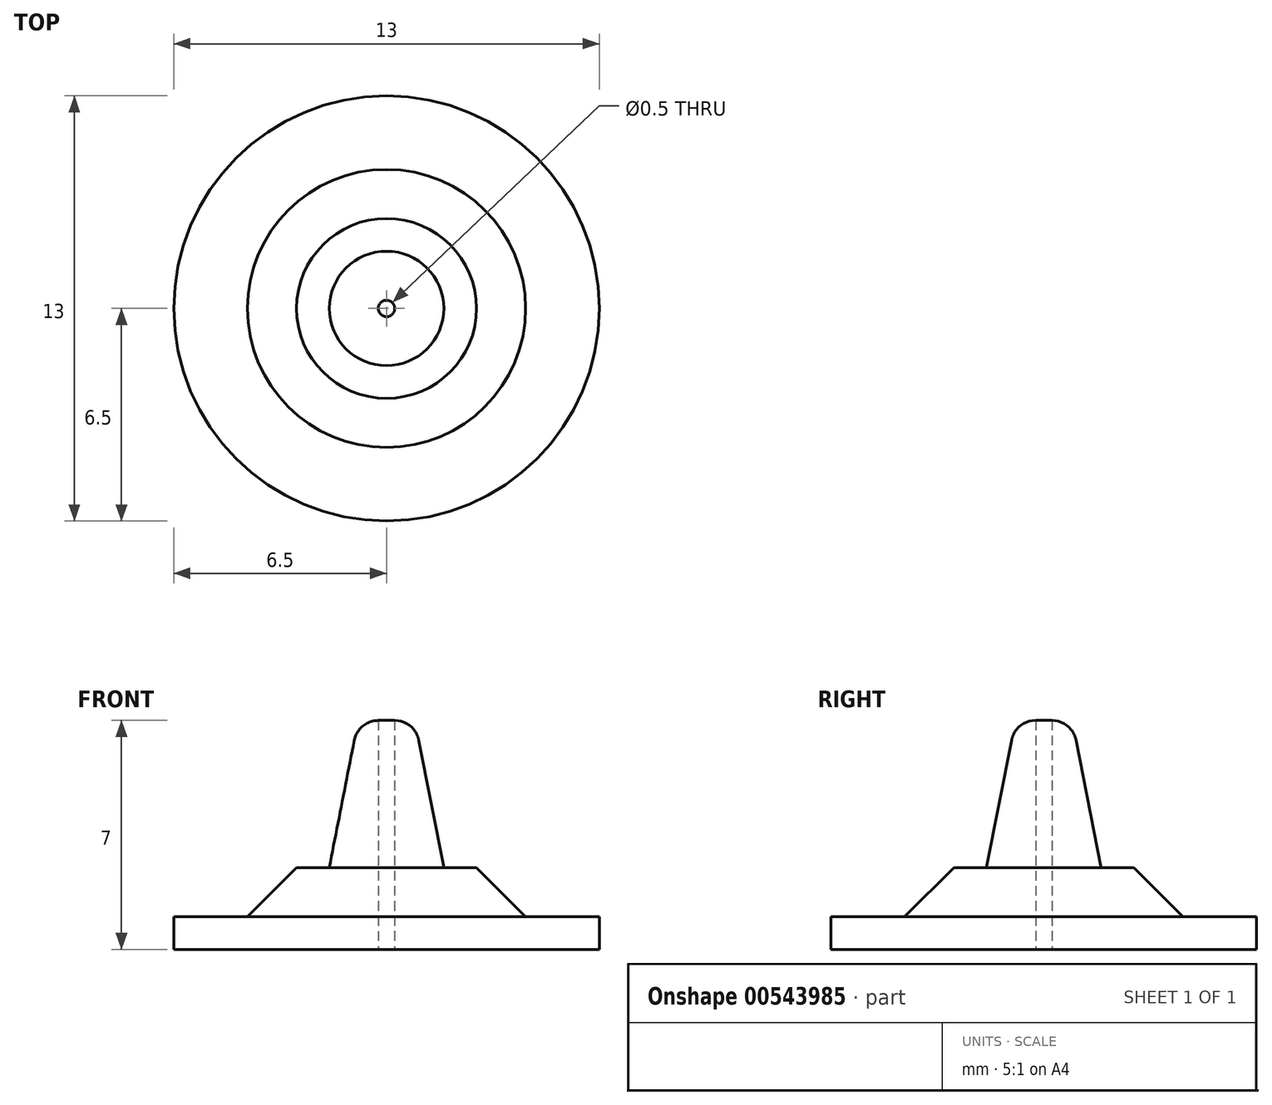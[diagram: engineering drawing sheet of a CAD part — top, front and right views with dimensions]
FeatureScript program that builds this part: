
annotation { "Feature Type Name" : "Feature", "Feature Type Description" : "" }
export const myFeature = defineFeature(function(context is Context, id is Id, definition is map)
    precondition{}
    {
        {
            var Q0;
            Q0=qCreatedBy(makeId("Front.planeOp"),FACE);
            var sketch = newSketch(context, id + "F0", { "sketchPlane" : qUnion([Q0])});
            skLineSegment(sketch, "E0", {"start": v(0.25, 0) * mm, "end": v(0.25, 7) * mm});
            skLineSegment(sketch, "E1", {"start": v(1.75, 2.5) * mm, "end": v(0.99, 6.4) * mm});
            skArc(sketch, "E2", {"start": v(0.99, 6.4) * mm, "mid": v(0.73, 6.83) * mm, "end": v(0.25, 7) * mm});
            skLineSegment(sketch, "E3", {"start": v(0, 0) * mm, "end": v(0, 8.8) * mm});
            skLineSegment(sketch, "E4", {"start": v(1.75, 2.5) * mm, "end": v(2.75, 2.5) * mm});
            skLineSegment(sketch, "E5", {"start": v(2.75, 2.5) * mm, "end": v(4.25, 1) * mm});
            skLineSegment(sketch, "E6", {"start": v(4.25, 1) * mm, "end": v(6.5, 1) * mm});
            skLineSegment(sketch, "E7", {"start": v(0.25, 0) * mm, "end": v(6.5, 0) * mm});
            skLineSegment(sketch, "E8", {"start": v(6.5, 0) * mm, "end": v(6.5, 1) * mm});
            skLineSegment(sketch, "E9", {"start": v(2.75, 2.5) * mm, "end": v(2.75, 1) * mm, "construction": true});
            skLineSegment(sketch, "E10", {"start": v(2.75, 1) * mm, "end": v(4.25, 1) * mm, "construction": true});
            skSolve(sketch);
        }
        {
            var Q0;
            Q0=makeQuery(id+"F0.imprint","IMPRINT",FACE,{"disambiguationData":[TD([[makeQuery(id+"F0.imprint","IMPRINT",EDGE,{"derivedFrom":sQuery(id+"F0.wireOp",EDGE,"E0")}),-1.0]])]});
            var Q1;
            Q1=sQuery(id+"F0.wireOp",EDGE,"E3");
            revolve(context, id + "F1", {"entities" : qUnion([Q0]), "axis" : qUnion([Q1]), "revolveType" : RevolveType.FULL});
        }
    });
